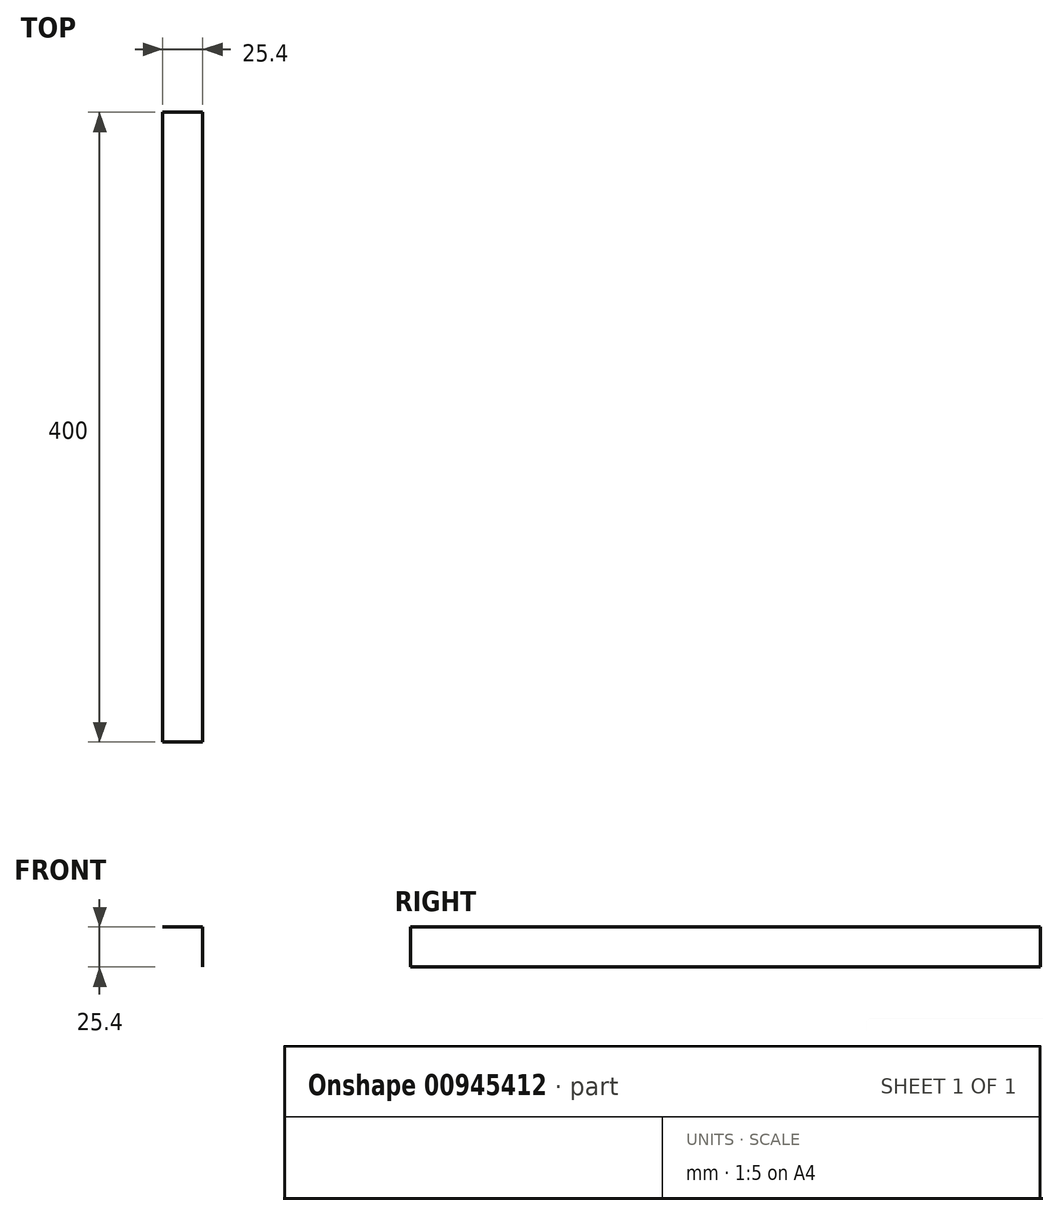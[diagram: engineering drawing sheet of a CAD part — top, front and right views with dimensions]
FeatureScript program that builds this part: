
annotation { "Feature Type Name" : "Feature", "Feature Type Description" : "" }
export const myFeature = defineFeature(function(context is Context, id is Id, definition is map)
    precondition{}
    {
        {
            var Q0;
            Q0=qCreatedBy(makeId("Front.planeOp"),FACE);
            var sketch = newSketch(context, id + "F0", { "sketchPlane" : qUnion([Q0])});
            skLineSegment(sketch, "E0.bottom", {"start": v(-45.77, 20.78) * mm, "end": v(-20.37, 20.78) * mm});
            skLineSegment(sketch, "E0.right", {"start": v(-20.37, 20.78) * mm, "end": v(-20.37, -4.62) * mm});
            skSolve(sketch);
        }
        {
            var Q0;
            Q0=sQuery(id+"F0.wireOp",EDGE,"E0.bottom");
            var Q1;
            Q1=sQuery(id+"F0.wireOp",EDGE,"E0.right");
            extrude(context, id + "F1", {"bodyType" : ToolBodyType.SURFACE, "surfaceEntities" : qUnion([Q0, Q1]), "depth" : 400 * mm, "offsetDistance" : 25.4 * mm});
        }
    });
